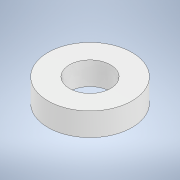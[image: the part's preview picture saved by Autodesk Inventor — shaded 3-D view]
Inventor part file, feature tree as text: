
AUTODESK INVENTOR PART (.ipt)
format: ipt  version: 2022.2 (Build 262287000, 287)  size: 101,376 bytes
history: native  units: in
note: dims shown in document units (in); Inventor stores cm internally (conversion verified against a paired STEP export)
features: extrude x1, sketch x1
ambient origin geometry x8: Origin, YZ Plane, XZ Plane, XY Plane, X Axis, Y Axis, Z Axis, Center Point
bodies: Solid1 (feature_tree)
feature tree (2):
  extrude  "Extrusion1"  Depth=0.275in
  sketch  "Sketch1"  dims[d0=0.49in d1=1.0in d2=0.275in d3=0.0in]
